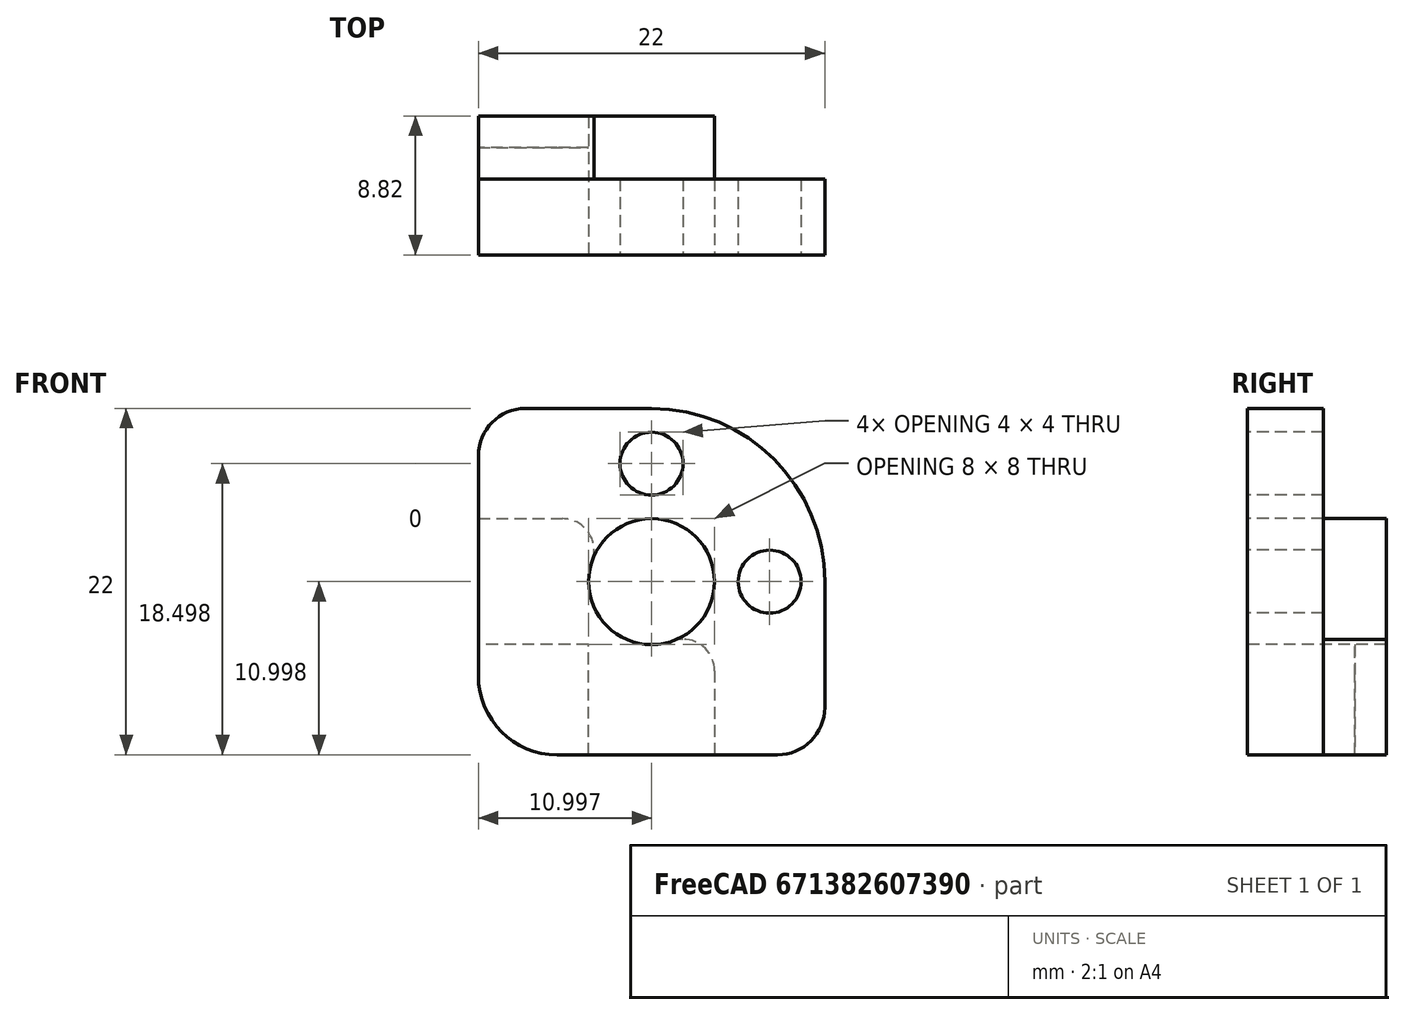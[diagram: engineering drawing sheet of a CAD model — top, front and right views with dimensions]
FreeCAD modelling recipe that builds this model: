
FCSTD DOCUMENT  (FreeCAD 0.16R4695 (Git))
Label: bed_corner_v2
License: All rights reserved
LicenseURL: http://en.wikipedia.org/wiki/All_rights_reserved
objects: Part::Feature×1, Sketcher::SketchObject×1, PartDesign::Pad×1
note: 4 computed .brp shape members not serialized (recipe doc carries the construction recipe); baked Part::Feature solids carry a one-line shape summary decoded from their .brp

FEATURE [Part::Feature] Part__Feature  label="TAZ_5_bed_assembly005"
  shape: bbox 22 x 8.825 x 22 mm, 25 faces (baked)
FEATURE [Sketcher::SketchObject] Sketch
  ExternalGeometry = -> [Part__Feature]
  Placement = pos=(0,-230.997,0) rot=(0,0.707107,0.707107;3.14159rad)
  Support = -> Part__Feature [Face6]
  sketch-geometry (5):
    g0: LineSegment StartX=-624.267 StartY=9.23757 StartZ=0 EndX=-624.267 EndY=11.2376 EndZ=0
    g1: LineSegment StartX=-624.267 StartY=11.2376 StartZ=0 EndX=-631.267 EndY=11.2376 EndZ=0
    g2: LineSegment StartX=-631.267 StartY=11.2376 StartZ=0 EndX=-631.267 EndY=4.23757 EndZ=0
    g3: LineSegment StartX=-631.267 StartY=4.23757 StartZ=0 EndX=-629.267 EndY=4.23757 EndZ=0
    g4: ArcOfCircle CenterX=-629.267 CenterY=9.23758 CenterZ=0 NormalX=0 NormalY=0 NormalZ=1 Radius=5.00001 StartAngle=4.71239 EndAngle=6.28318
  constraints (12):
    c: Coincident(g-4,g0)
    c: Coincident(g0,g-4)
    c: Coincident(g0,g1)
    c: Coincident(g1,g-3)
    c: Coincident(g1,g2)
    c: Vertical(g2)
    c: Coincident(g2,g3)
    c: Coincident(g3,g-5)
    c: Horizontal(g3)
    c: Coincident(g4,g0)
    c: Coincident(g3,g4)
    c: Tangent(g4,g-5)
FEATURE [PartDesign::Pad] Pad
  Length = 2
  Length2 = 100
  Sketch = -> Sketch
  Type = 0
